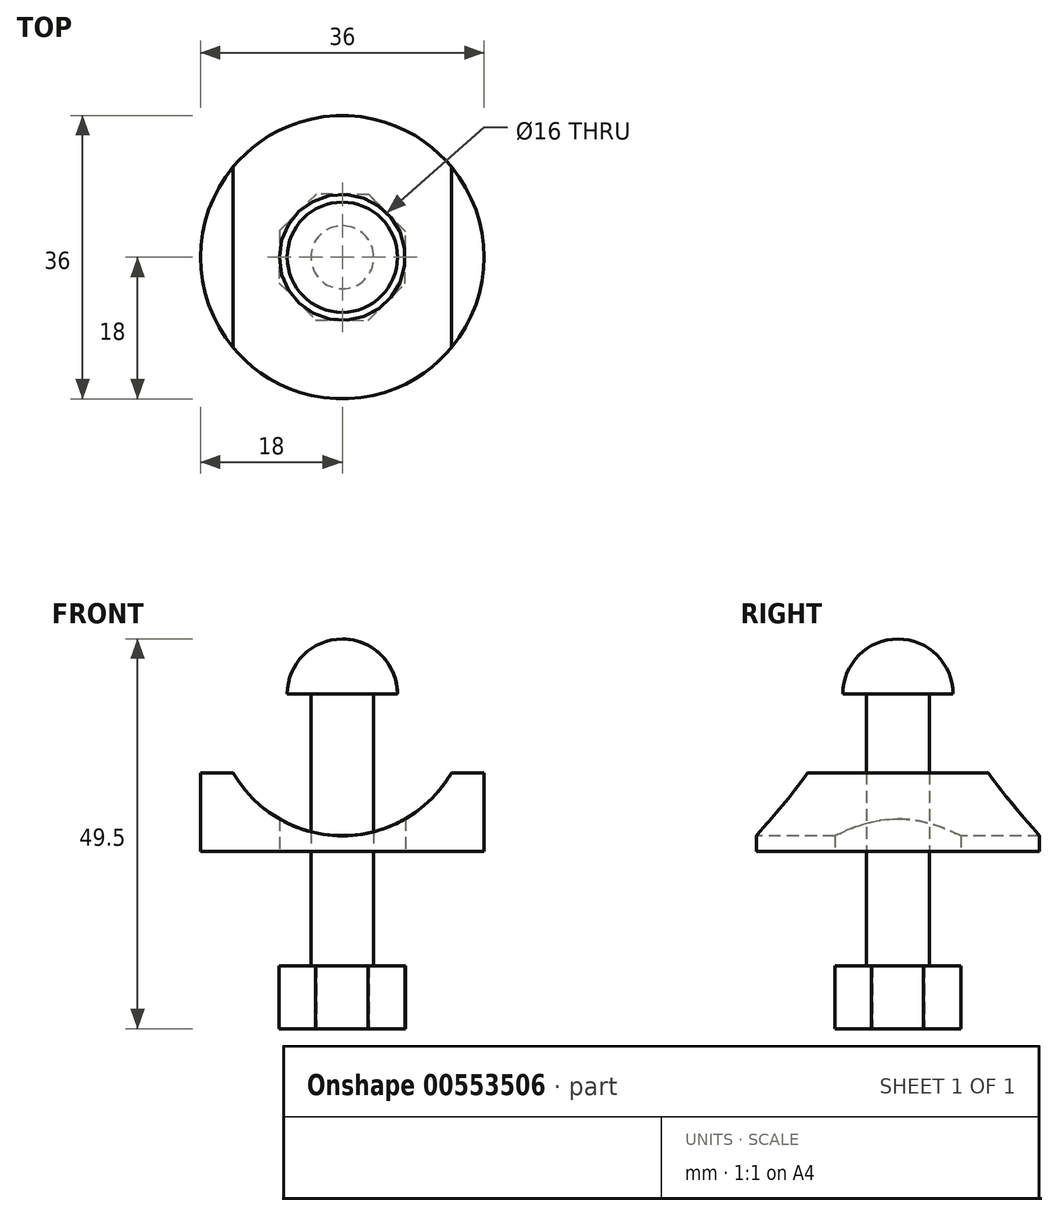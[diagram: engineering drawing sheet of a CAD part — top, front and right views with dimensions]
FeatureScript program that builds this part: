
annotation { "Feature Type Name" : "Feature", "Feature Type Description" : "" }
export const myFeature = defineFeature(function(context is Context, id is Id, definition is map)
    precondition{}
    {
        {
            var Q0;
            Q0=qCreatedBy(makeId("Top.planeOp"),FACE);
            var sketch = newSketch(context, id + "F0", { "sketchPlane" : qUnion([Q0])});
            skCircle(sketch, "E0", {"center": v(0, 0) * mm, "radius": 18 * mm});
            skCircle(sketch, "E1.0", {"center": v(0, 0) * mm, "radius": 8 * mm});
            skSolve(sketch);
        }
        {
            var Q0;
            Q0 = qSketchRegion(id + "F0", true);
            extrude(context, id + "F1", {"entities" : qUnion([Q0]), "depth" : 10 * mm, "offsetDistance" : 25 * mm});
        }
        {
            var Q0;
            Q0=qCreatedBy(makeId("Front.planeOp"),FACE);
            var sketch = newSketch(context, id + "F2", { "sketchPlane" : qUnion([Q0])});
            skCircle(sketch, "E2", {"center": v(0, 18) * mm, "radius": 16 * mm});
            skSolve(sketch);
        }
        {
            var Q0;
            Q0 = qSketchRegion(id + "F2", true);
            extrude(context, id + "F3", {"entities" : qUnion([Q0]), "operationType" : NewBodyOperationType.REMOVE, "oppositeDirection" : true, "depth" : 25 * mm, "offsetDistance" : 25 * mm, "hasSecondDirection" : true, "secondDirectionOppositeDirection" : false, "secondDirectionDepth" : 25 * mm});
        }
        {
            var Q0;
            Q0=qCreatedBy(makeId("Top.planeOp"),FACE);
            var sketch = newSketch(context, id + "F4", { "sketchPlane" : qUnion([Q0])});
            skCircle(sketch, "E3", {"center": v(0, 0) * mm, "radius": 4 * mm});
            skSolve(sketch);
        }
        {
            var Q0;
            Q0=qCreatedBy(makeId("Front.planeOp"),FACE);
            var sketch = newSketch(context, id + "F5", { "sketchPlane" : qUnion([Q0])});
            skLineSegment(sketch, "E4", {"start": v(0, 20) * mm, "end": v(-7, 20) * mm});
            skArc(sketch, "E5", {"start": v(-7, 20) * mm, "mid": v(-4.95, 24.95) * mm, "end": v(0, 27) * mm});
            skLineSegment(sketch, "E6", {"start": v(0, 20) * mm, "end": v(0, 44.89) * mm, "construction": true});
            skPoint(sketch, "E7.orphan", {"position": v(7, 20) * mm});
            skLineSegment(sketch, "E8", {"start": v(0, 27) * mm, "end": v(0, 20) * mm});
            skSolve(sketch);
        }
        {
            var Q0;
            Q0 = qSketchRegion(id + "F4", true);
            extrude(context, id + "F6", {"entities" : qUnion([Q0]), "depth" : 45 * mm, "offsetDistance" : 25 * mm, "hasSecondDirection" : true, "secondDirectionOppositeDirection" : true, "secondDirectionDepth" : 25 * mm, "symmetric" : true});
        }
        {
            var Q0;
            Q0=makeQuery(id+"F5.imprint","IMPRINT",FACE,{"disambiguationData":[TD([[makeQuery(id+"F5.imprint","IMPRINT",EDGE,{"derivedFrom":sQuery(id+"F5.wireOp",EDGE,"E4")}),-1.0]])]});
            var Q1;
            Q1=sQuery(id+"F5.wireOp",EDGE,"E5");
            var Q2;
            Q2=sQuery(id+"F5.wireOp",EDGE,"E4");
            var Q3;
            Q3=sQuery(id+"F5.wireOp",EDGE,"xyxgrDlj-IXyP-q8LC-yVf6-eW5lwFyHAGQl");
            var Q4;
            Q4=sQuery(id+"F5.wireOp",EDGE,"E6");
            revolve(context, id + "F7", {"operationType" : NewBodyOperationType.ADD, "surfaceOperationType" : NewSurfaceOperationType.ADD, "entities" : qUnion([Q0]), "surfaceEntities" : qUnion([Q1, Q2, Q3]), "axis" : qUnion([Q4]), "revolveType" : RevolveType.FULL});
        }
        {
            var Q0;
            Q0=makeQuery(id+"F6.opExtrude","CAP_FACE",FACE,{"disambiguationData":[OSD([sQuery(id+"F4.wireOp",EDGE,"E3")])],"isStart":true});
            var sketch = newSketch(context, id + "F8", { "sketchPlane" : qUnion([Q0])});
            skCircle(sketch, "E9.cCircle", {"center": v(0, 0) * mm, "radius": 8 * mm, "construction": true});
            skLineSegment(sketch, "E9.0", {"start": v(3.25, 8.03) * mm, "end": v(7.97, 3.37) * mm});
            skLineSegment(sketch, "E9.1", {"start": v(7.97, 3.37) * mm, "end": v(8.03, -3.25) * mm});
            skLineSegment(sketch, "E9.2", {"start": v(8.03, -3.25) * mm, "end": v(3.37, -7.97) * mm});
            skLineSegment(sketch, "E9.3", {"start": v(3.37, -7.97) * mm, "end": v(-3.25, -8.03) * mm});
            skLineSegment(sketch, "E9.4", {"start": v(-3.25, -8.03) * mm, "end": v(-7.97, -3.37) * mm});
            skLineSegment(sketch, "E9.5", {"start": v(-7.97, -3.37) * mm, "end": v(-8.03, 3.25) * mm});
            skLineSegment(sketch, "E9.6", {"start": v(-8.03, 3.25) * mm, "end": v(-3.37, 7.97) * mm});
            skLineSegment(sketch, "E9.7", {"start": v(-3.37, 7.97) * mm, "end": v(3.25, 8.03) * mm});
            skPoint(sketch, "E9.0.midPoint", {"position": v(5.61, 5.7) * mm});
            skSolve(sketch);
        }
        {
            var Q0;
            Q0 = qSketchRegion(id + "F8", true);
            extrude(context, id + "F9", {"entities" : qUnion([Q0]), "operationType" : NewBodyOperationType.ADD, "oppositeDirection" : true, "depth" : 8 * mm, "offsetDistance" : 25 * mm});
        }
    });
